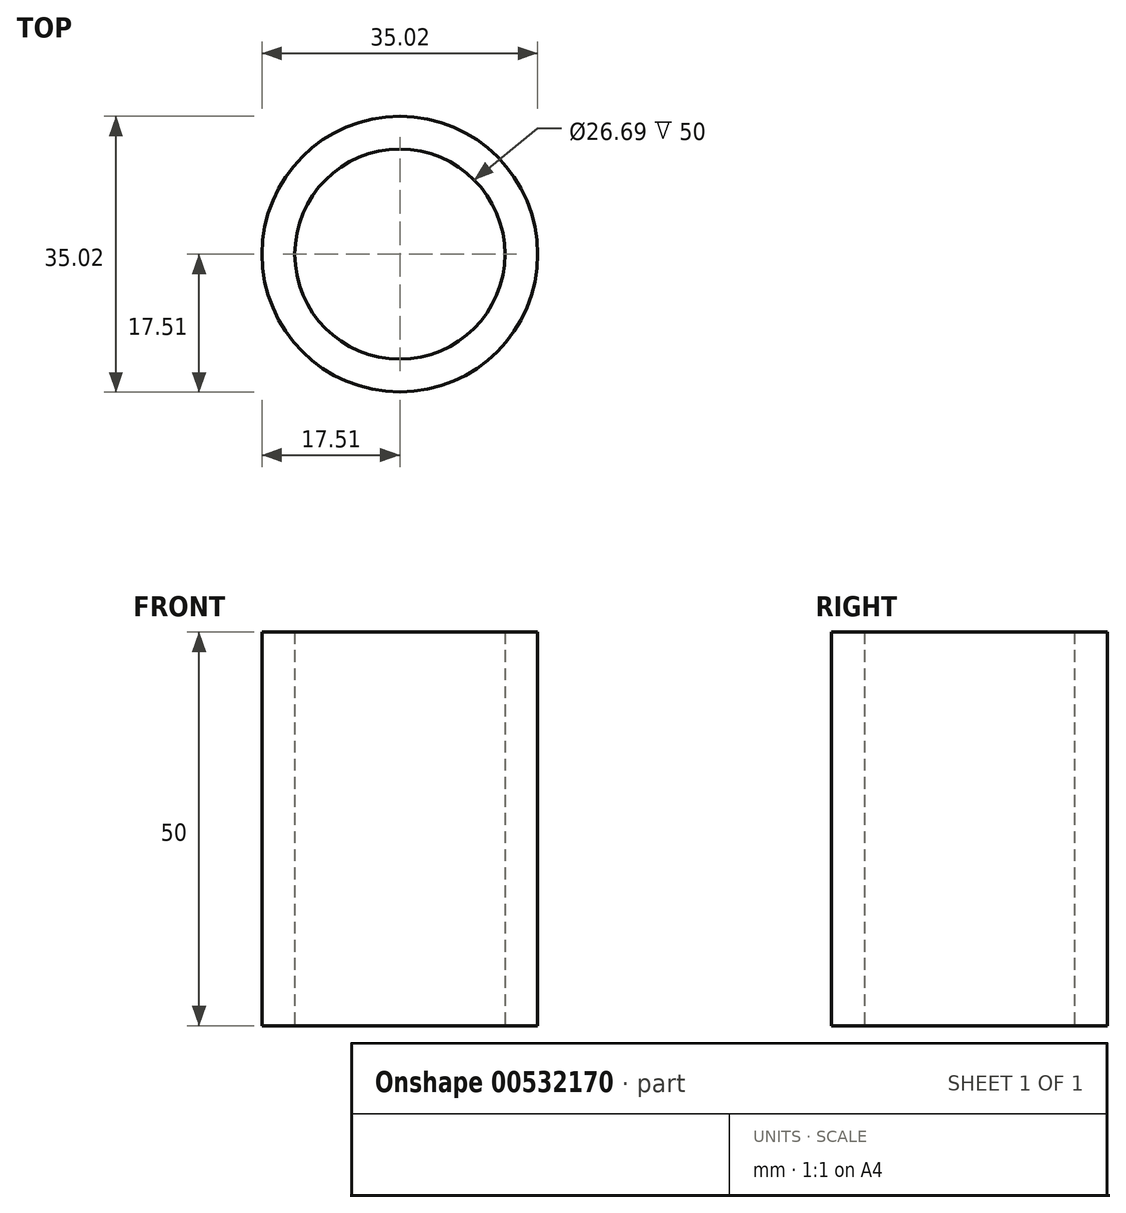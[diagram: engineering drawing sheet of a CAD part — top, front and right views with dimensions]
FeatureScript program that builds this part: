
annotation { "Feature Type Name" : "Feature", "Feature Type Description" : "" }
export const myFeature = defineFeature(function(context is Context, id is Id, definition is map)
    precondition{}
    {
        {
            var Q0;
            Q0=qCreatedBy(makeId("Top.planeOp"),FACE);
            var sketch = newSketch(context, id + "F0", { "sketchPlane" : qUnion([Q0])});
            skCircle(sketch, "E0", {"center": v(0, 0) * mm, "radius": 17.51 * mm});
            skCircle(sketch, "E1", {"center": v(0, 0) * mm, "radius": 13.34 * mm});
            skSolve(sketch);
        }
        {
            var Q0;
            Q0 = qSketchRegion(id + "F0", true);
            extrude(context, id + "F1", {"entities" : qUnion([Q0]), "depth" : 50 * mm, "offsetDistance" : 25 * mm});
        }
    });
